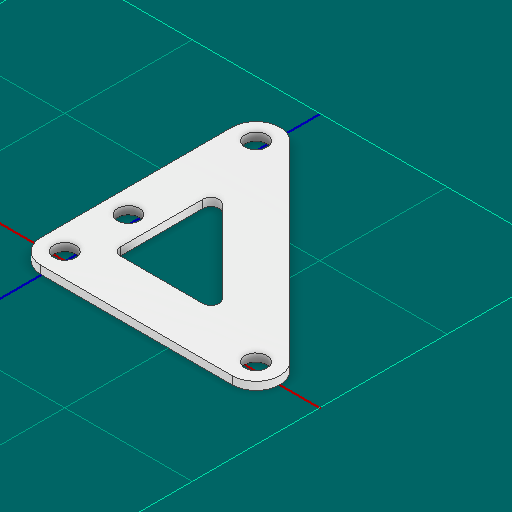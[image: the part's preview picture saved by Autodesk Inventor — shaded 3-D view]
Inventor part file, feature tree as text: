
AUTODESK INVENTOR PART (.ipt)
format: ipt  version: 2025 (Build 290162000, 162)  size: 138,752 bytes
history: native  units: in
note: dims shown in document units (in); Inventor stores cm internally (conversion verified against a paired STEP export)
features: other x6, sketch x1
ambient origin geometry x8: Origin, YZ Plane, XZ Plane, XY Plane, X Axis, Y Axis, Z Axis, Center Point
bodies: Solid1 (feature_tree)
feature tree (7):
  other  "right_angle_gusset.ipt"
  other  "Blocks"
  other  "main"
  other  "Solid1::right_angle_gusset.ipt"
  other  "TaggingFeature1"
  sketch  "Sketch1"  dims[d0=0.3937in d1=0.375in d2=0.375in d5=0.375in d6=0.0625in d7=0.0625in d11=0.172in]
  other  "main:1"
